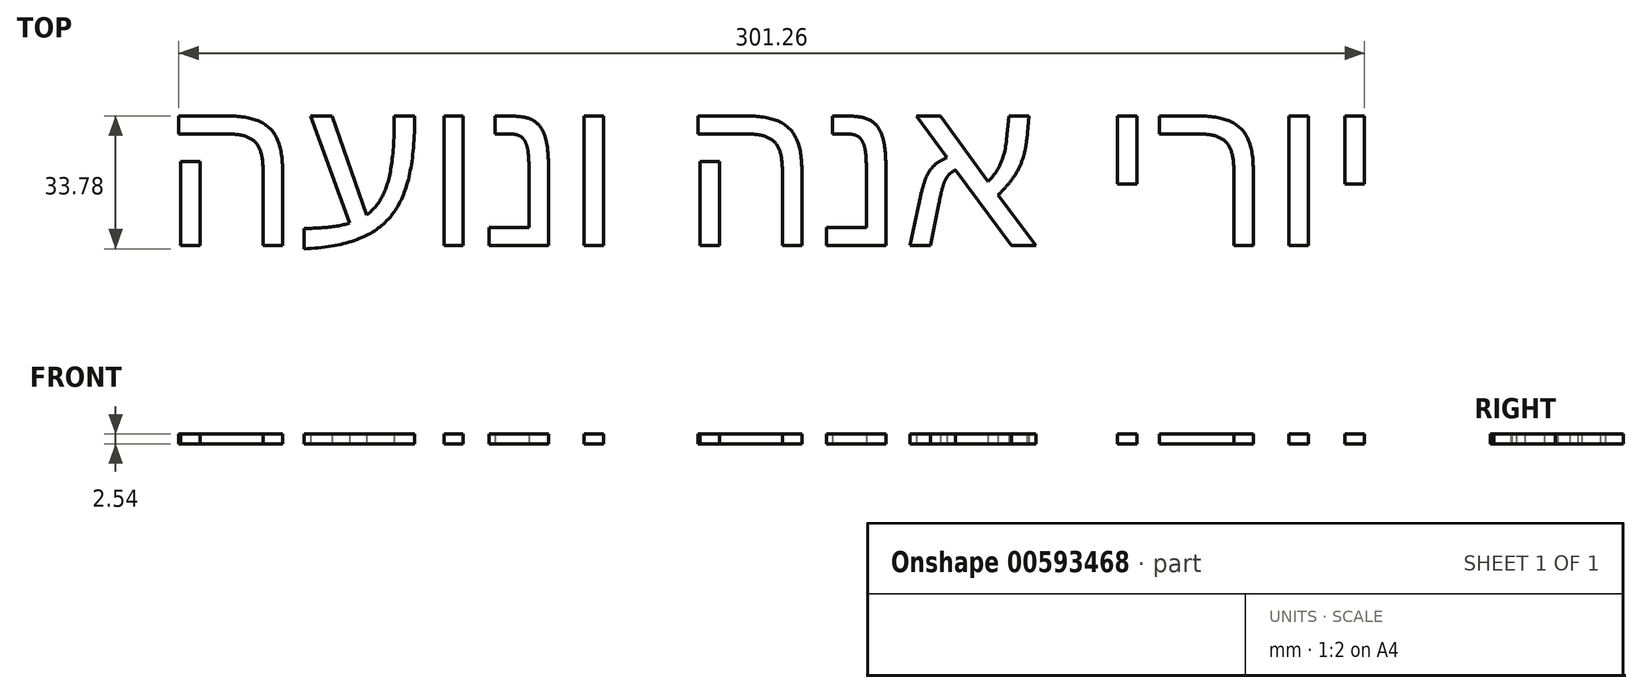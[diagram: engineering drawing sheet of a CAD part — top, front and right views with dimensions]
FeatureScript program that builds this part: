
annotation { "Feature Type Name" : "Feature", "Feature Type Description" : "" }
export const myFeature = defineFeature(function(context is Context, id is Id, definition is map)
    precondition{}
    {
        {
            var Q0;
            Q0=qCreatedBy(makeId("Top.planeOp"),FACE);
            var sketch = newSketch(context, id + "F0", { "sketchPlane" : qUnion([Q0])});
            skText(sketch, "E0", { "text": "העונו הנא ירוי", "fontName": "Arimo-Regular.ttf"});
            const initialGuessF0  = {"E0": [-0.05532, -0.02293, 1, 0, 0.03954]};
            skSetInitialGuess(sketch, initialGuessF0);
            skSolve(sketch);
        }
        {
            var Q0;
            Q0 = qSketchRegion(id + "F0", true);
            extrude(context, id + "F1", {"entities" : qUnion([Q0]), "depth" : 2.54 * mm, "offsetDistance" : 25.4 * mm});
        }
    });
